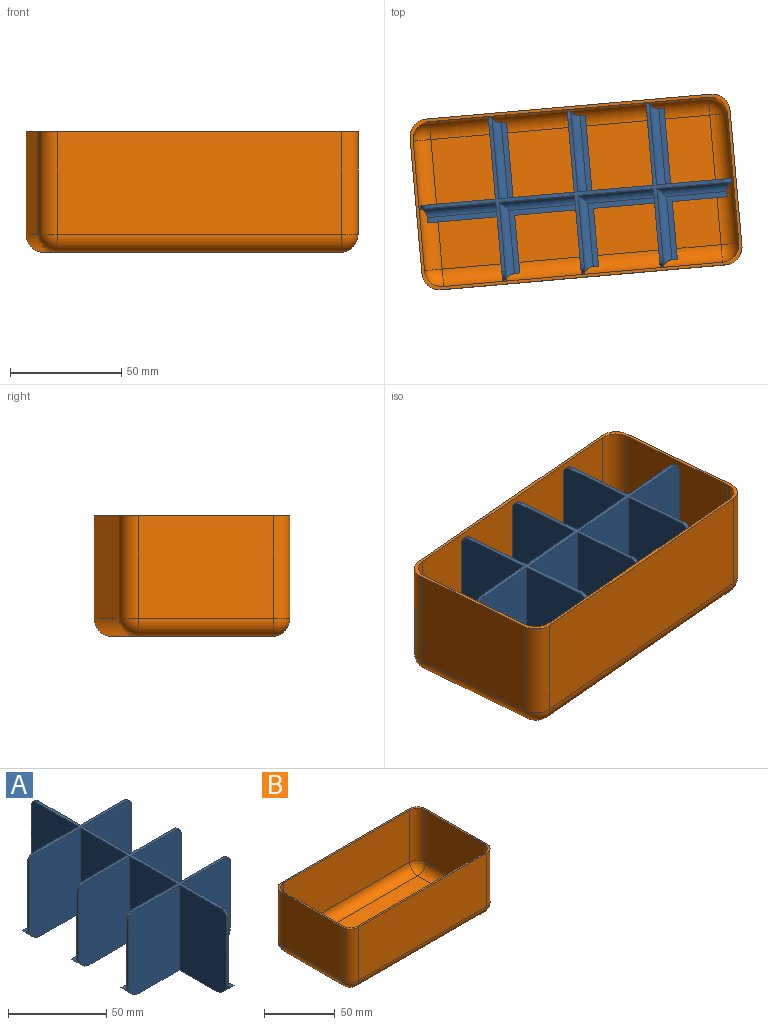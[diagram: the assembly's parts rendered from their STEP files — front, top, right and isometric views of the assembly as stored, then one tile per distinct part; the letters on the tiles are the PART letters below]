
ASSEMBLY  parts=2 mates=1
PART A: 73 faces, bbox 73.5x140.7x53 mm
  f0: plane 27.6x2mm, normal (1,0,0), area 55.2mm2, adj f8,f15,f36,f43
  f1: plane 31.24x2mm, normal (1,0,0), area 59.2mm2, adj f2,f15,f45,f54
  f2: plane 31.24x2.4mm, normal (0,0,1), area 75mm2, adj f1,f45,f54,f55
  f3: plane 47x34mm, normal (1,0,0), area 1598mm2, adj f17,f36,f44,f60
  f4: plane 47x33.95mm, normal (1,0,0), area 1592mm2, adj f17,f18,f45,f54,f55,f72
  f5: plane 53x34mm, normal (-1,0,0), area 1785.8mm2, adj f15,f17,f33,f39,f40,f41,f62
  f6: plane 53x33.95mm, normal (-1,0,0), area 1782.2mm2, adj f15,f17,f18,f42,f54,f72
  f7: plane 27.6x2mm, normal (1,0,0), area 55.2mm2, adj f12,f15,f27,f34
  f8: plane 30x28.44mm, normal (0,0,1), area 134.5mm2, adj f0,f36,f43,f48,f60,f61
  f9: plane 47x34mm, normal (1,0,0), area 1598mm2, adj f17,f27,f35,f58
  f10: plane 53x34mm, normal (-1,0,0), area 1785.8mm2, adj f15,f17,f24,f30,f31,f32,f63
  f11: plane 24.84x2mm, normal (1,0,0), area 46.4mm2, adj f15,f16,f25,f53
  f12: plane 30x28.44mm, normal (0,0,1), area 134.5mm2, adj f7,f27,f34,f50,f58,f59
  f13: plane 47x33.95mm, normal (1,0,0), area 1592mm2, adj f17,f19,f26,f53,f56,f71
  f14: plane 53x33.95mm, normal (-1,0,0), area 1765.9mm2, adj f15,f17,f19,f21,f22,f23,f53,f64
  f15: plane 124.7x57.5mm, normal (0,0,-1), area 2185.6mm2, adj f0,f1,f5,f6,f7,f10,f11,f14
  f16: plane 28.44x27.24mm, normal (0,0,1), area 127.9mm2, adj f11,f25,f52,f53,f56,f57
  f17: plane 132.7x65.5mm, normal (0,0,1), area 519mm2, adj f3,f4,f5,f6,f9,f10,f13,f14
  f18: plane 41x1.6mm, normal (0,-1,0), area 65.6mm2, adj f4,f6,f54,f72
  f19: plane 41x1.6mm, normal (0,1,0), area 65.6mm2, adj f13,f14,f53,f71
  f20: plane 41x1.6mm, normal (-1,0,0), area 65.6mm2, adj f21,f24,f51,f69
  f21: plane 47x36.75mm, normal (0,1,0), area 1723.6mm2, adj f14,f17,f20,f51,f64,f69
  f22: plane 34.04x2.4mm, normal (0,0,1), area 81.7mm2, adj f14,f23,f51,f64
  f23: plane 34.04x2mm, normal (0,1,0), area 64.8mm2, adj f14,f15,f22,f51
  f24: plane 53x36.75mm, normal (0,-1,0), area 1930.6mm2, adj f10,f15,f17,f20,f51,f69
  f25: plane 26.04x2mm, normal (0,1,0), area 48.8mm2, adj f11,f15,f16,f52
  f26: plane 47x35.15mm, normal (0,1,0), area 1648.4mm2, adj f13,f17,f28,f52,f57,f70
  f27: plane 53x35.15mm, normal (0,-1,0), area 1829.5mm2, adj f7,f9,f12,f15,f17,f28,f52,f58
  f28: plane 41x1.6mm, normal (1,0,0), area 65.6mm2, adj f26,f27,f52,f70
  f29: plane 41x1.6mm, normal (-1,0,0), area 65.6mm2, adj f30,f33,f49,f67
  f30: plane 47x36.75mm, normal (0,1,0), area 1723.6mm2, adj f10,f17,f29,f49,f63,f67
  f31: plane 34.04x2.4mm, normal (0,0,1), area 81.7mm2, adj f10,f32,f49,f63
  f32: plane 34.04x2mm, normal (0,1,0), area 64.8mm2, adj f10,f15,f31,f49
  f33: plane 53x36.75mm, normal (0,-1,0), area 1930.6mm2, adj f5,f15,f17,f29,f49,f67
  f34: plane 26.04x2mm, normal (0,1,0), area 48.8mm2, adj f7,f12,f15,f50
  f35: plane 47x35.15mm, normal (0,1,0), area 1648.4mm2, adj f9,f17,f37,f50,f59,f68
  f36: plane 53x35.15mm, normal (0,-1,0), area 1829.5mm2, adj f0,f3,f8,f15,f17,f37,f50,f60
  f37: plane 41x1.6mm, normal (1,0,0), area 65.6mm2, adj f35,f36,f50,f68
  f38: plane 41x1.6mm, normal (-1,0,0), area 65.6mm2, adj f39,f42,f47,f65
  f39: plane 47x36.75mm, normal (0,1,0), area 1723.6mm2, adj f5,f17,f38,f47,f62,f65
  f40: plane 34.04x2.4mm, normal (0,0,1), area 81.7mm2, adj f5,f41,f47,f62
  f41: plane 34.04x2mm, normal (0,1,0), area 64.8mm2, adj f5,f15,f40,f47
  f42: plane 53x36.75mm, normal (0,-1,0), area 1930.6mm2, adj f6,f15,f17,f38,f47,f65
  f43: plane 26.04x2mm, normal (0,1,0), area 48.8mm2, adj f0,f8,f15,f48
  f44: plane 47x35.15mm, normal (0,1,0), area 1648.4mm2, adj f3,f17,f46,f48,f61,f66
  f45: plane 53x35.15mm, normal (0,-1,0), area 1829.5mm2, adj f1,f2,f4,f15,f17,f46,f48,f55
  f46: plane 41x1.6mm, normal (1,0,0), area 65.6mm2, adj f44,f45,f48,f66
  f47: cylinder r=8mm len=8mm, axis (0,1,0), area 61.7mm2, adj f15,f38,f39,f40,f41,f42,f62
  f48: cylinder r=8mm len=8mm, axis (0,-1,0), area 61.7mm2, adj f8,f15,f43,f44,f45,f46,f61
  f49: cylinder r=8mm len=8mm, axis (0,1,0), area 61.7mm2, adj f15,f29,f30,f31,f32,f33,f63
  f50: cylinder r=8mm len=8mm, axis (0,-1,0), area 61.7mm2, adj f12,f15,f34,f35,f36,f37,f59
  f51: cylinder r=8mm len=8mm, axis (0,1,0), area 61.7mm2, adj f15,f20,f21,f22,f23,f24,f64
  f52: cylinder r=8mm len=8mm, axis (0,-1,0), area 61.7mm2, adj f15,f16,f25,f26,f27,f28,f57
  f53: cylinder r=8mm len=8mm, axis (1,0,0), area 61.7mm2, adj f11,f13,f14,f15,f16,f19,f56
  f54: cylinder r=8mm len=8mm, axis (-1,0,0), area 61.7mm2, adj f1,f2,f4,f6,f15,f18,f55
  f55: cylinder r=4mm len=33.7mm, axis (0,1,0), area 203.4mm2, adj f2,f4,f45,f54
  f56: cylinder r=4mm len=33.7mm, axis (0,1,0), area 194.2mm2, adj f13,f16,f53,f57
  f57: cylinder r=4mm len=34.9mm, axis (-1,0,0), area 201.8mm2, adj f16,f26,f52,f56
  f58: cylinder r=4mm len=34mm, axis (0,1,0), area 204.5mm2, adj f9,f12,f27,f59
  f59: cylinder r=4mm len=34.9mm, axis (-1,0,0), area 201.8mm2, adj f12,f35,f50,f58
  f60: cylinder r=4mm len=34mm, axis (0,1,0), area 204.5mm2, adj f3,f8,f36,f61
  f61: cylinder r=4mm len=34.9mm, axis (-1,0,0), area 201.8mm2, adj f8,f44,f48,f60
  f62: cylinder r=4mm len=36.5mm, axis (-1,0,0), area 220.9mm2, adj f5,f39,f40,f47
  f63: cylinder r=4mm len=36.5mm, axis (-1,0,0), area 220.9mm2, adj f10,f30,f31,f49
  f64: cylinder r=4mm len=36.5mm, axis (-1,0,0), area 220.9mm2, adj f14,f21,f22,f51
  f65: cylinder r=4mm len=4mm, axis (0,-1,0), area 10.1mm2, adj f17,f38,f39,f42
  f66: cylinder r=4mm len=4mm, axis (0,1,0), area 10.1mm2, adj f17,f44,f45,f46
  f67: cylinder r=4mm len=4mm, axis (0,-1,0), area 10.1mm2, adj f17,f29,f30,f33
  f68: cylinder r=4mm len=4mm, axis (0,1,0), area 10.1mm2, adj f17,f35,f36,f37
  f69: cylinder r=4mm len=4mm, axis (0,-1,0), area 10.1mm2, adj f17,f20,f21,f24
  f70: cylinder r=4mm len=4mm, axis (0,1,0), area 10.1mm2, adj f17,f26,f27,f28
  f71: cylinder r=4mm len=4mm, axis (-1,0,0), area 10.1mm2, adj f13,f14,f17,f19
  f72: cylinder r=4mm len=4mm, axis (1,0,0), area 10.1mm2, adj f4,f6,f17,f18
PART B: 35 faces, bbox 144.6x77.1x54.3 mm
  f0: plane 61.1x46.3mm, normal (1,0,0), area 2828.9mm2, adj f8,f13,f16,f26
  f1: plane 128.6x46.3mm, normal (0,1,0), area 5954.2mm2, adj f8,f13,f14,f22
  f2: plane 61.1x46.3mm, normal (-1,0,0), area 2828.9mm2, adj f8,f14,f15,f19
  f3: plane 58.5x45mm, normal (1,0,0), area 2632.5mm2, adj f8,f9,f12,f32
  f4: plane 126x45mm, normal (0,-1,0), area 5670mm2, adj f8,f9,f10,f28
  f5: plane 58.5x45mm, normal (-1,0,0), area 2632.5mm2, adj f8,f10,f11,f29
  f6: plane 126x45mm, normal (0,1,0), area 5670mm2, adj f8,f11,f12,f33
  f7: plane 128.6x46.3mm, normal (0,-1,0), area 5954.2mm2, adj f8,f15,f16,f23
  f8: plane 144.6x77.1mm, normal (0,0,1), area 569.7mm2, adj f0,f1,f2,f3,f4,f5,f6,f7
  f9: cylinder r=8mm len=45mm, axis (0,0,-1), area 565.5mm2, adj f3,f4,f8,f30
  f10: cylinder r=8mm len=45mm, axis (0,0,1), area 565.5mm2, adj f4,f5,f8,f27
  f11: cylinder r=8mm len=45mm, axis (0,0,-1), area 565.5mm2, adj f5,f6,f8,f31
  f12: cylinder r=8mm len=45mm, axis (0,0,1), area 565.5mm2, adj f3,f6,f8,f34
  f13: cylinder r=8mm len=46.3mm, axis (0,0,-1), area 581.8mm2, adj f0,f1,f8,f24
  f14: cylinder r=8mm len=46.3mm, axis (0,0,1), area 581.8mm2, adj f1,f2,f8,f20
  f15: cylinder r=8mm len=46.3mm, axis (0,0,-1), area 581.8mm2, adj f2,f7,f8,f21
  f16: cylinder r=8mm len=46.3mm, axis (0,0,1), area 581.8mm2, adj f0,f7,f8,f25
  f17: plane 126x58.5mm, normal (0,0,1), area 7371mm2, adj f28,f29,f32,f33
  f18: plane 128.6x61.1mm, normal (0,0,-1), area 7857.5mm2, adj f19,f22,f23,f26
  f19: cylinder r=8mm len=61.1mm, axis (0,-1,0), area 767.8mm2, adj f2,f18,f20,f21
  f20: sphere r=8mm, area 100.5mm2, adj f14,f19,f22
  f21: sphere r=8mm, area 100.5mm2, adj f15,f19,f23
  f22: cylinder r=8mm len=128.6mm, axis (-1,0,0), area 1616mm2, adj f1,f18,f20,f24
  f23: cylinder r=8mm len=128.6mm, axis (1,0,0), area 1616mm2, adj f7,f18,f21,f25
  f24: sphere r=8mm, area 100.5mm2, adj f13,f22,f26
  f25: sphere r=8mm, area 100.5mm2, adj f16,f23,f26
  f26: cylinder r=8mm len=61.1mm, axis (0,1,0), area 767.8mm2, adj f0,f18,f24,f25
  f27: sphere r=8mm, area 100.5mm2, adj f10,f28,f29
  f28: cylinder r=8mm len=126mm, axis (1,0,0), area 1583.4mm2, adj f4,f17,f27,f30
  f29: cylinder r=8mm len=58.5mm, axis (0,-1,0), area 735.1mm2, adj f5,f17,f27,f31
  f30: sphere r=8mm, area 100.5mm2, adj f9,f28,f32
  f31: sphere r=8mm, area 100.5mm2, adj f11,f29,f33
  f32: cylinder r=8mm len=58.5mm, axis (0,1,0), area 735.1mm2, adj f3,f17,f30,f34
  f33: cylinder r=8mm len=126mm, axis (-1,0,0), area 1583.4mm2, adj f6,f17,f31,f34
  f34: sphere r=8mm, area 100.5mm2, adj f12,f32,f33
PLACE A rot(axis=(0,0,-1),85deg) t=(-0.85,4.73,-15.91)mm
PLACE B rot(axis=(0,0,1),5deg) t=(-0.85,4.73,-15.91)mm
MATE revolute A.f15 <-> B.f17  axis (0,0,1) through (-0.85,4.73,-15.91)mm
